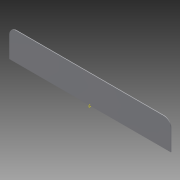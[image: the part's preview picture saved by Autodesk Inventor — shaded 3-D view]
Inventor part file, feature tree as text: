
AUTODESK INVENTOR PART (.ipt)
format: ipt  version: 2013 (Build 170138000, 138)  size: 74,752 bytes
history: native  units: in
note: dims shown in document units (in); Inventor stores cm internally (conversion verified against a paired STEP export)
features: other x3, sketch x1, plane x1
ambient origin geometry x8: Origin, YZ Plane, XZ Plane, XY Plane, X Axis, Y Axis, Z Axis, Center Point
bodies: Solid1 (feature_tree)
feature tree (5):
  other  "FE00036Shelf.ipt"
  other  "Solid1::FE00036Shelf.ipt"
  other  "TaggingFeature1"
  sketch  "Sketch1"  dims[d0=0.3937in d1=12.0in d2=0.25in d3=0.0in d4=3.0in]
  plane  "Work Plane1"
